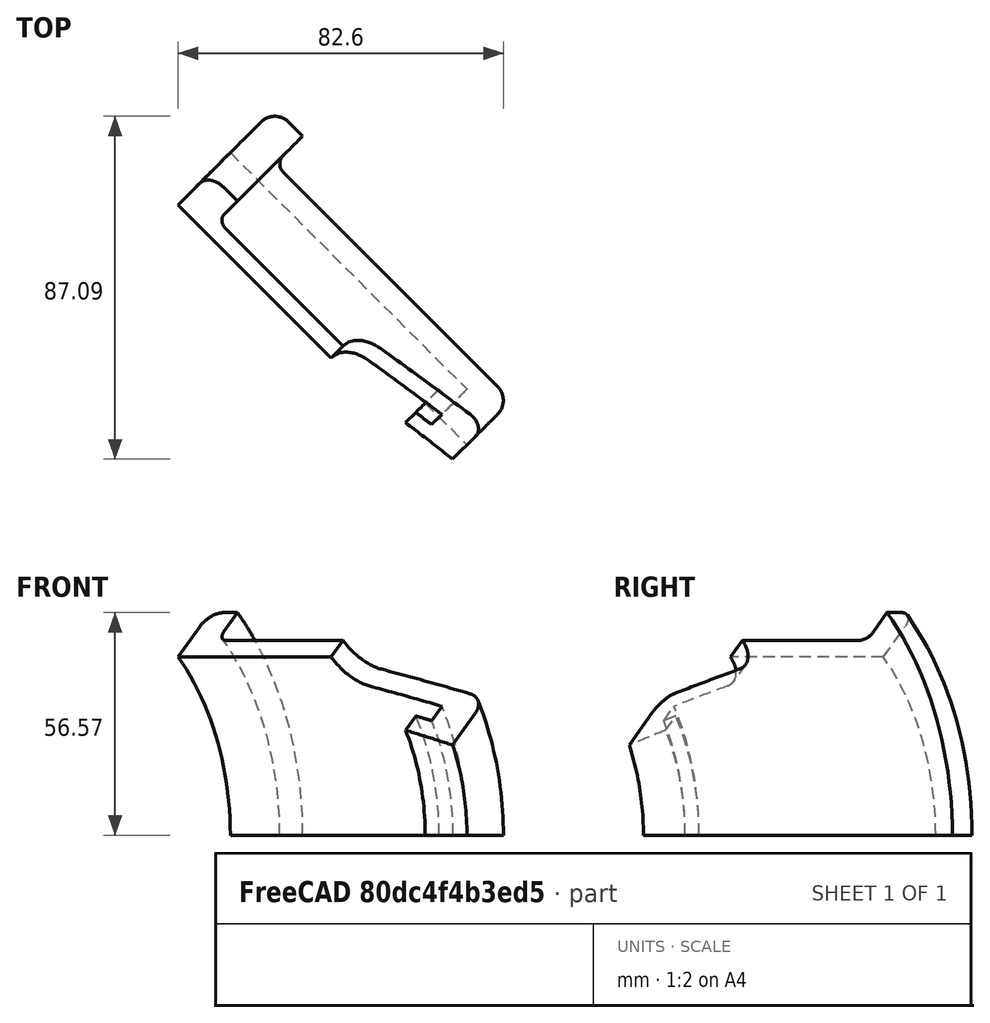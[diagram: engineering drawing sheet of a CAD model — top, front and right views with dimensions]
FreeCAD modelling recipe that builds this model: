
FCSTD DOCUMENT  (FreeCAD 0.15R4671 (Git))
Label: sphere_support_cyls4_w1
License: All rights reserved
LicenseURL: http://en.wikipedia.org/wiki/All_rights_reserved
objects: Part::Cut×11, Part::Box×8, Part::Cylinder×6, Part::Fillet×3, Part::MultiFuse×2
note: 30 computed .brp shape members not serialized (recipe doc carries the construction recipe); baked Part::Feature solids carry a one-line shape summary decoded from their .brp

FEATURE [Part::Cylinder] Cylinder  label="Base_Cylinder"
  Angle = 360
  Height = 10
  Radius = 80
FEATURE [Part::Cylinder] Cylinder001  label="Body_Cylinder"
  Angle = 360
  Height = 90
  Placement = pos=(0,0,5) rot=(0,0,1;0rad)
  Radius = 70
FEATURE [Part::MultiFuse] Fusion  label="Core_Fusion"
  Shapes = -> [Cylinder,Cylinder001]
FEATURE [Part::Cylinder] Cylinder002  label="Inner_Hole"
  Angle = 360
  Height = 85
  Radius = 64
FEATURE [Part::Cut] Cut
  Base = -> Fusion
  Tool = -> Cylinder002
FEATURE [Part::Cylinder] Cylinder003  label="Inner_Lip"
  Angle = 360
  Height = 10
  Placement = pos=(0,0,80) rot=(0,0,1;0rad)
  Radius = 59
FEATURE [Part::MultiFuse] Fusion001
  Shapes = -> [Cut,Cylinder003]
FEATURE [Part::Cylinder] Cylinder004  label="Through_Hole"
  Angle = 360
  Height = 100
  Radius = 54
FEATURE [Part::Cut] Cut001
  Base = -> Fusion001
  Tool = -> Cylinder004
FEATURE [Part::Fillet] Fillet
  Base = -> Cut001
  Edges = 1 edges r=3: [Edge12]
FEATURE [Part::Fillet] Fillet001
  Base = -> Fillet
  Edges = 1 edges r=5: [Edge11]
FEATURE [Part::Fillet] Fillet002
  Base = -> Fillet001
  Edges = 1 edges r=5: [Edge13]
FEATURE [Part::Cylinder] Cylinder005  label="Bearing_Holes"
  Angle = 360
  Height = 180
  Placement = pos=(0,90,65) rot=(1,0,0;1.5708rad)
  Radius = 10
FEATURE [Part::Cut] Cut002
  Base = -> Fillet002
  Tool = -> Cylinder005
FEATURE [Part::Box] Box  label="Bearing_Slot"
  Height = 35
  Length = 20
  Placement = pos=(-10,48,65) rot=(0,0,1;0rad)
  Width = 25
FEATURE [Part::Cut] Cut003
  Base = -> Cut002
  Tool = -> Box
FEATURE [Part::Box] Box001  label="Cube"
  Height = 35
  Length = 10
  Placement = pos=(0,48,65) rot=(0,1,0;0.261799rad)
  Width = 25
FEATURE [Part::Cut] Cut004
  Base = -> Cut003
  Tool = -> Box001
FEATURE [Part::Box] Box002  label="Cube001"
  Height = 35
  Length = 10
  Placement = pos=(-9.95,48,64) rot=(0,-1,0;0.261799rad)
  Width = 25
FEATURE [Part::Cut] Cut005
  Base = -> Cut004
  Tool = -> Box002
FEATURE [Part::Box] Box003  label="Tab_Cut_R"
  Height = 80
  Length = 20
  Placement = pos=(63,-10,20) rot=(0,0,1;0rad)
  Width = 20
FEATURE [Part::Cut] Cut006
  Base = -> Cut005
  Tool = -> Box003
FEATURE [Part::Box] Box004  label="Tab_Cut_L"
  Height = 80
  Length = 20
  Placement = pos=(-83,-10,20) rot=(0,0,1;0rad)
  Width = 20
FEATURE [Part::Cut] Cut007
  Base = -> Cut006
  Placement = pos=(0,0,0) rot=(0.707107,0.707107,0;1.5708rad)
  Tool = -> Box004
FEATURE [Part::Box] Box005  label="Cube002"
  Height = 100
  Length = 200
  Placement = pos=(-70,-120,-100) rot=(0,0,1;0rad)
  Width = 200
FEATURE [Part::Cut] Cut008
  Base = -> Cut007
  Placement = pos=(0,0,0) rot=(-0.707107,-0.707107,0;1.5708rad)
  Tool = -> Box005
FEATURE [Part::Box] Box006  label="Cube003"
  Height = 100
  Length = 100
  Placement = pos=(0,0,0) rot=(0,0,1;1.5708rad)
  Width = 100
FEATURE [Part::Cut] Cut009
  Base = -> Cut008
  Tool = -> Box006
FEATURE [Part::Box] Box007  label="Cube004"
  Height = 100
  Length = 100
  Placement = pos=(0,0,0) rot=(0,0,1;3.14159rad)
  Width = 100
FEATURE [Part::Cut] Cut010
  Base = -> Cut009
  Placement = pos=(0,0,0) rot=(0.707107,0.707107,0;1.5708rad)
  Tool = -> Box007
